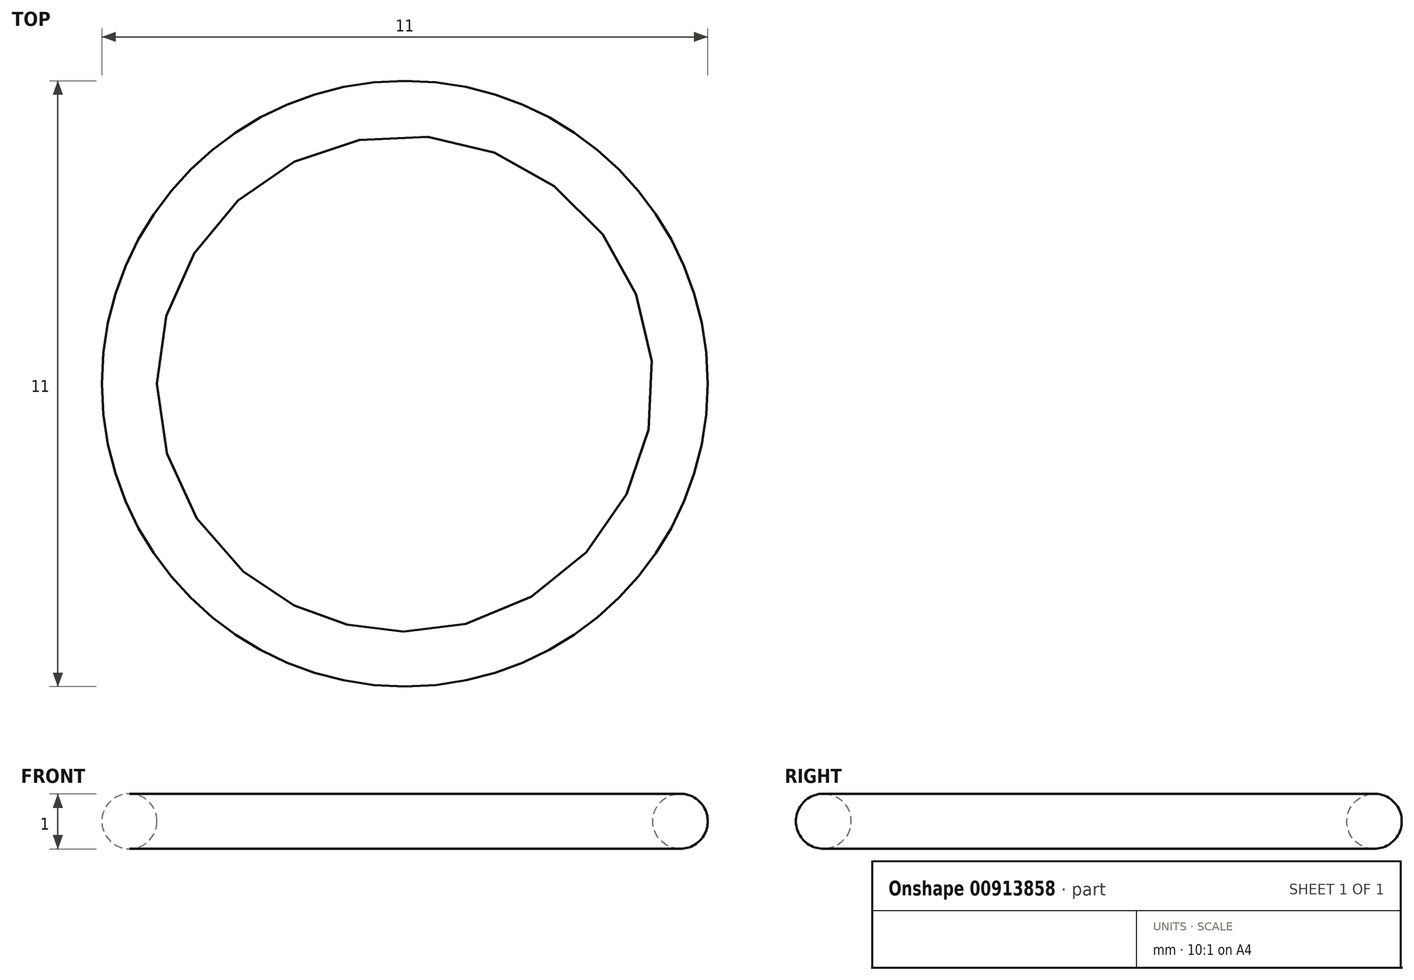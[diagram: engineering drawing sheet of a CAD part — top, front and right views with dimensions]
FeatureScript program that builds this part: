
annotation { "Feature Type Name" : "Feature", "Feature Type Description" : "" }
export const myFeature = defineFeature(function(context is Context, id is Id, definition is map)
    precondition{}
    {
        {
            var Q0;
            Q0=qCreatedBy(makeId("Front.planeOp"),FACE);
            var sketch = newSketch(context, id + "F0", { "sketchPlane" : qUnion([Q0])});
            skLineSegment(sketch, "E0", {"start": v(0, 0) * mm, "end": v(0, 67.62) * mm, "construction": true});
            skCircle(sketch, "E1", {"center": v(-5, 4.03) * mm, "radius": 0.5 * mm});
            skLineSegment(sketch, "E2", {"start": v(-4.5, 4.03) * mm, "end": v(-5.5, 4.03) * mm, "construction": true});
            skSolve(sketch);
        }
        {
            var Q0;
            Q0=makeQuery(id+"F0.imprint","IMPRINT",FACE,{"disambiguationData":[TD([[makeQuery(id+"F0.imprint","IMPRINT",EDGE,{"derivedFrom":sQuery(id+"F0.wireOp",EDGE,"uiM048YO-4fzq-UUJt-prhe-HZhT9VTXhxak")}),1.0]])]});
            var Q1;
            Q1=makeQuery(id+"F0.imprint","IMPRINT",FACE,{"disambiguationData":[TD([[makeQuery(id+"F0.imprint","IMPRINT",EDGE,{"derivedFrom":sQuery(id+"F0.wireOp",EDGE,"GFbKmP1q-Tj7D-fgYK-uiMn-HIncw07lXcZm.bottom")}),-1.0]])]});
            var Q2;
            Q2=makeQuery(id+"F0.imprint","IMPRINT",FACE,{"disambiguationData":[TD([[makeQuery(id+"F0.imprint","IMPRINT",EDGE,{"derivedFrom":sQuery(id+"F0.wireOp",EDGE,"E1")}),1.0]])]});
            var Q3;
            Q3=sQuery(id+"F0.wireOp",EDGE,"E0");
            revolve(context, id + "F1", {"surfaceOperationType" : NewSurfaceOperationType.NEW, "entities" : qUnion([Q0, Q1, Q2]), "axis" : qUnion([Q3]), "revolveType" : RevolveType.FULL});
        }
    });
